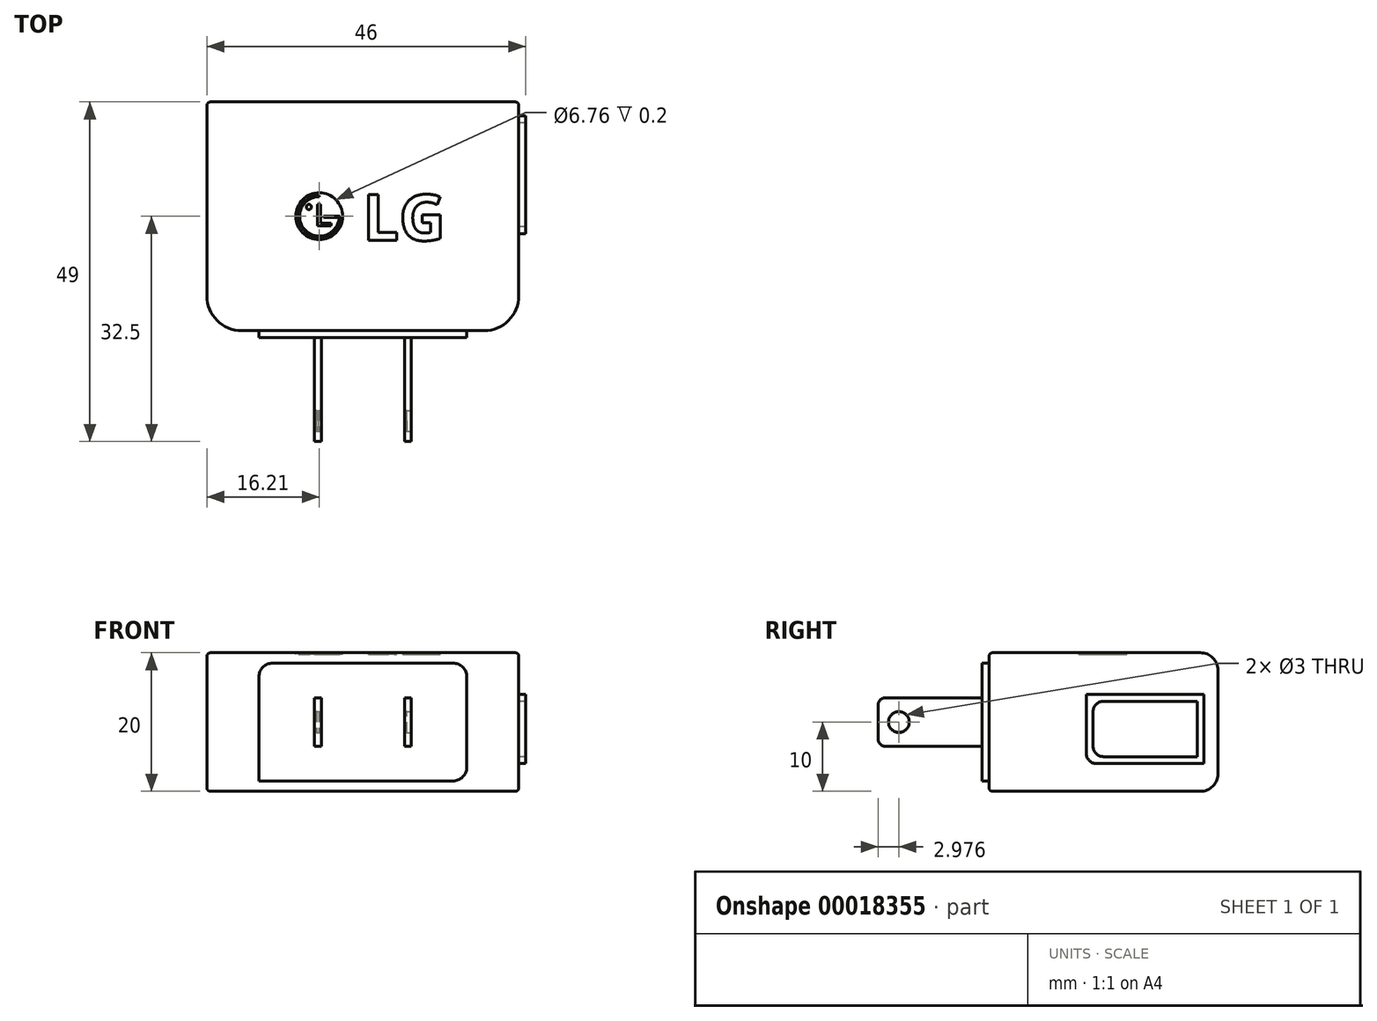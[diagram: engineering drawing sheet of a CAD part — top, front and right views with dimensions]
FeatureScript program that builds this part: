
annotation { "Feature Type Name" : "Feature", "Feature Type Description" : "" }
export const myFeature = defineFeature(function(context is Context, id is Id, definition is map)
    precondition{}
    {
        {
            var Q0;
            Q0=qCreatedBy(makeId("Top.planeOp"),FACE);
            var sketch = newSketch(context, id + "F0", { "sketchPlane" : qUnion([Q0])});
            skLineSegment(sketch, "E0.rect.bottom", {"start": v(22.5, 16.5) * mm, "end": v(-22.5, 16.5) * mm});
            skLineSegment(sketch, "E0.rect.top", {"start": v(22.5, -16.5) * mm, "end": v(-22.5, -16.5) * mm});
            skLineSegment(sketch, "E0.rect.left", {"start": v(22.5, 16.5) * mm, "end": v(22.5, -16.5) * mm});
            skLineSegment(sketch, "E0.rect.right", {"start": v(-22.5, 16.5) * mm, "end": v(-22.5, -16.5) * mm});
            skPoint(sketch, "E0.rect.middle", {"position": v(0, 0) * mm});
            skSolve(sketch);
        }
        {
            var Q0;
            Q0=makeQuery(id+"F0.imprint","IMPRINT",FACE,{"disambiguationData":[TD([[makeQuery(id+"F0.imprint","IMPRINT",EDGE,{"derivedFrom":sQuery(id+"F0.wireOp",EDGE,"E0.rect.bottom")}),1.0]])]});
            extrude(context, id + "F1", {"entities" : qUnion([Q0]), "depth" : 20 * mm});
        }
        {
            var Q0;
            Q0=makeQuery(id+"F1.opExtrude","SWEPT_FACE",FACE,{"disambiguationData":[OSD([sQuery(id+"F0.wireOp",EDGE,"E0.rect.top")])]});
            var sketch = newSketch(context, id + "F2", { "sketchPlane" : qUnion([Q0])});
            skLineSegment(sketch, "E1", {"start": v(0, 0) * mm, "end": v(0, 1.5) * mm});
            skLineSegment(sketch, "E2", {"start": v(0, 1.5) * mm, "end": v(-15, 1.5) * mm});
            skLineSegment(sketch, "E3.MirrorCS", {"start": v(0, 1.5) * mm, "end": v(15, 1.5) * mm});
            skLineSegment(sketch, "E4", {"start": v(-15, 1.5) * mm, "end": v(-15, 18.5) * mm});
            skLineSegment(sketch, "E5.MirrorCS", {"start": v(15, 1.5) * mm, "end": v(15, 18.5) * mm});
            skLineSegment(sketch, "E6", {"start": v(-15, 18.5) * mm, "end": v(15, 18.5) * mm});
            skLineSegment(sketch, "E7.bottom", {"start": v(-15, 1.5) * mm, "end": v(-7, 1.5) * mm});
            skLineSegment(sketch, "E7.left", {"start": v(-15, 1.5) * mm, "end": v(-15, 6.5) * mm});
            skLineSegment(sketch, "E8.bottom", {"start": v(-7, 6.5) * mm, "end": v(-6, 6.5) * mm});
            skLineSegment(sketch, "E8.top", {"start": v(-7, 13.5) * mm, "end": v(-6, 13.5) * mm});
            skLineSegment(sketch, "E8.left", {"start": v(-7, 6.5) * mm, "end": v(-7, 13.5) * mm});
            skLineSegment(sketch, "E8.right", {"start": v(-6, 6.5) * mm, "end": v(-6, 13.5) * mm});
            skLineSegment(sketch, "E9.MirrorCS", {"start": v(6, 6.5) * mm, "end": v(6, 13.5) * mm});
            skLineSegment(sketch, "E10.MirrorCS", {"start": v(7, 6.5) * mm, "end": v(7, 13.5) * mm});
            skLineSegment(sketch, "E11.MirrorCS", {"start": v(7, 6.5) * mm, "end": v(6, 6.5) * mm});
            skLineSegment(sketch, "E12.MirrorCS", {"start": v(7, 13.5) * mm, "end": v(6, 13.5) * mm});
            skSolve(sketch);
        }
        {
            var Q0;
            Q0=makeQuery(id+"F2.imprint","IMPRINT",FACE,{"disambiguationData":[TD([[makeQuery(id+"F2.imprint","IMPRINT",EDGE,{"derivedFrom":sQuery(id+"F2.wireOp",EDGE,"E2")}),-1.0]])]});
            extrude(context, id + "F3", {"entities" : qUnion([Q0]), "operationType" : NewBodyOperationType.ADD, "depth" : 1 * mm});
        }
        {
            var Q0;
            Q0=makeQuery(id+"F3.boolean.opBoolean","SPLIT",FACE,{"disambiguationData":[TD([makeQuery(id+"F3.opExtrude","SWEPT_FACE",FACE,{"disambiguationData":[OSD([sQuery(id+"F2.wireOp",EDGE,"E8.bottom")])]})])],"derivedFrom":makeQuery(id+"F1.opExtrude","SWEPT_FACE",FACE,{"disambiguationData":[OSD([sQuery(id+"F0.wireOp",EDGE,"E0.rect.top")])]})});
            var Q1;
            Q1=makeQuery(id+"F3.boolean.opBoolean","SPLIT",FACE,{"disambiguationData":[TD([makeQuery(id+"F3.opExtrude","SWEPT_FACE",FACE,{"disambiguationData":[OSD([sQuery(id+"F2.wireOp",EDGE,"E9.MirrorCS")])]})])],"derivedFrom":makeQuery(id+"F1.opExtrude","SWEPT_FACE",FACE,{"disambiguationData":[OSD([sQuery(id+"F0.wireOp",EDGE,"E0.rect.top")])]})});
            extrude(context, id + "F4", {"entities" : qUnion([Q0, Q1]), "operationType" : NewBodyOperationType.ADD, "depth" : 16 * mm});
        }
        {
            var Q0;
            Q0=makeQuery(id+"F4.opExtrude","CAP_EDGE",EDGE,{"disambiguationData":[OSD([sQuery(id+"F2.wireOp",EDGE,"E8.top")])],"isStart":false});
            var Q1;
            Q1=makeQuery(id+"F4.opExtrude","CAP_EDGE",EDGE,{"disambiguationData":[OSD([sQuery(id+"F2.wireOp",EDGE,"E8.bottom")])],"isStart":false});
            var Q2;
            Q2=makeQuery(id+"F4.opExtrude","CAP_EDGE",EDGE,{"disambiguationData":[OSD([sQuery(id+"F2.wireOp",EDGE,"E11.MirrorCS")])],"isStart":false});
            var Q3;
            Q3=makeQuery(id+"F4.opExtrude","CAP_EDGE",EDGE,{"disambiguationData":[OSD([sQuery(id+"F2.wireOp",EDGE,"E12.MirrorCS")])],"isStart":false});
            fillet(context, id + "F5", {"entities" : qUnion([Q0, Q1, Q2, Q3]), "radius" : 1 * mm, "tangentPropagation" : true, "allowEdgeOverflow" : false});
        }
        {
            var Q0;
            Q0=makeQuery(id+"F3.opExtrude","SWEPT_EDGE",EDGE,{"disambiguationData":[OSD([sQuery(id+"F2.wireOp",EDGE,"E5.MirrorCS"),sQuery(id+"F2.wireOp",EDGE,"E6")])]});
            var Q1;
            Q1=makeQuery(id+"F3.opExtrude","SWEPT_EDGE",EDGE,{"disambiguationData":[OSD([sQuery(id+"F2.wireOp",EDGE,"E4"),sQuery(id+"F2.wireOp",EDGE,"E6")])]});
            var Q2;
            Q2=makeQuery(id+"F3.opExtrude","SWEPT_EDGE",EDGE,{"disambiguationData":[OSD([sQuery(id+"F2.wireOp",EDGE,"E3.MirrorCS"),sQuery(id+"F2.wireOp",EDGE,"E5.MirrorCS")])]});
            var Q3;
            Q3=makeQuery(id+"F3.opExtrude","SWEPT_EDGE",EDGE,{"disambiguationData":[OSD([sQuery(id+"F2.wireOp",EDGE,"E7.bottom"),sQuery(id+"F2.wireOp",EDGE,"E7.left")])]});
            fillet(context, id + "F6", {"entities" : qUnion([Q0, Q1, Q2, Q3]), "radius" : 2 * mm, "tangentPropagation" : true, "allowEdgeOverflow" : false});
        }
        {
            var Q0;
            Q0=makeQuery(id+"F1.opExtrude","SWEPT_FACE",FACE,{"disambiguationData":[OSD([sQuery(id+"F0.wireOp",EDGE,"E0.rect.left")])]});
            var sketch = newSketch(context, id + "F7", { "sketchPlane" : qUnion([Q0])});
            skLineSegment(sketch, "E13", {"start": v(14.5, 14) * mm, "end": v(14.5, 4) * mm});
            skLineSegment(sketch, "E14", {"start": v(-2.5, 4) * mm, "end": v(14.5, 4) * mm});
            skLineSegment(sketch, "E15", {"start": v(14.5, 14) * mm, "end": v(-2.5, 14) * mm});
            skLineSegment(sketch, "E16", {"start": v(-2.5, 14) * mm, "end": v(-2.5, 4) * mm});
            skLineSegment(sketch, "E17.bottom", {"start": v(-2.5, 14) * mm, "end": v(-1.5, 14) * mm});
            skLineSegment(sketch, "E17.left", {"start": v(-2.5, 14) * mm, "end": v(-2.5, 13) * mm});
            skLineSegment(sketch, "E18.bottom", {"start": v(14.5, 4) * mm, "end": v(13.5, 4) * mm});
            skLineSegment(sketch, "E18.left", {"start": v(14.5, 4) * mm, "end": v(14.5, 5) * mm});
            skLineSegment(sketch, "E19.bottom", {"start": v(-1.5, 13) * mm, "end": v(13.5, 13) * mm});
            skLineSegment(sketch, "E19.top", {"start": v(-1.5, 5) * mm, "end": v(13.5, 5) * mm});
            skLineSegment(sketch, "E19.left", {"start": v(-1.5, 13) * mm, "end": v(-1.5, 5) * mm});
            skLineSegment(sketch, "E19.right", {"start": v(13.5, 13) * mm, "end": v(13.5, 5) * mm});
            skSolve(sketch);
        }
        {
            var Q0;
            Q0 = qSketchRegion(id + "F7", true);
            extrude(context, id + "F8", {"entities" : qUnion([Q0]), "operationType" : NewBodyOperationType.ADD, "depth" : 1 * mm});
        }
        {
            var Q0;
            Q0=makeQuery(id+"F8.opExtrude","SWEPT_EDGE",EDGE,{"disambiguationData":[OSD([sQuery(id+"F7.wireOp",EDGE,"E17.bottom"),sQuery(id+"F7.wireOp",EDGE,"E17.left")])]});
            var Q1;
            Q1=makeQuery(id+"F8.opExtrude","SWEPT_EDGE",EDGE,{"disambiguationData":[OSD([sQuery(id+"F7.wireOp",EDGE,"E14"),sQuery(id+"F7.wireOp",EDGE,"E16")])]});
            var Q2;
            Q2=makeQuery(id+"F8.opExtrude","SWEPT_EDGE",EDGE,{"disambiguationData":[OSD([sQuery(id+"F7.wireOp",EDGE,"E19.top"),sQuery(id+"F7.wireOp",EDGE,"E19.left")])]});
            var Q3;
            Q3=makeQuery(id+"F8.opExtrude","SWEPT_EDGE",EDGE,{"disambiguationData":[OSD([sQuery(id+"F7.wireOp",EDGE,"E19.bottom"),sQuery(id+"F7.wireOp",EDGE,"E19.left")])]});
            fillet(context, id + "F9", {"entities" : qUnion([Q0, Q1, Q2, Q3]), "radius" : 1.5 * mm, "tangentPropagation" : true, "allowEdgeOverflow" : false});
        }
        {
            var Q0;
            Q0=makeQuery(id+"F1.opExtrude","CAP_EDGE",EDGE,{"disambiguationData":[OSD([sQuery(id+"F0.wireOp",EDGE,"E0.rect.bottom")])],"isStart":false});
            var Q1;
            Q1=makeQuery(id+"F1.opExtrude","CAP_EDGE",EDGE,{"disambiguationData":[OSD([sQuery(id+"F0.wireOp",EDGE,"E0.rect.bottom")])],"isStart":true});
            fillet(context, id + "F10", {"entities" : qUnion([Q0, Q1]), "radius" : 2.5 * mm, "tangentPropagation" : true, "allowEdgeOverflow" : false});
        }
        {
            var Q0;
            Q0=makeQuery(id+"F1.opExtrude","SWEPT_EDGE",EDGE,{"disambiguationData":[OSD([sQuery(id+"F0.wireOp",EDGE,"E0.rect.top"),sQuery(id+"F0.wireOp",EDGE,"E0.rect.left")])]});
            var Q1;
            Q1=makeQuery(id+"F1.opExtrude","SWEPT_EDGE",EDGE,{"disambiguationData":[OSD([sQuery(id+"F0.wireOp",EDGE,"E0.rect.top"),sQuery(id+"F0.wireOp",EDGE,"E0.rect.right")])]});
            fillet(context, id + "F11", {"entities" : qUnion([Q0, Q1]), "radius" : 5 * mm, "tangentPropagation" : true, "allowEdgeOverflow" : false});
        }
        {
            var Q0;
            Q0=makeQuery(id+"F1.opExtrude","CAP_EDGE",EDGE,{"disambiguationData":[OSD([sQuery(id+"F0.wireOp",EDGE,"E0.rect.top")])],"isStart":false});
            var Q1;
            {var subQ0=sQuery(id+"F0.wireOp",EDGE,"E0.rect.top");var subQ1=sQuery(id+"F0.wireOp",EDGE,"E0.rect.left");Q1=makeQuery(id+"F11.opFillet","BLEND_EDGE",EDGE,{"blendedFrom":[makeQuery(id+"F1.opExtrude","SWEPT_EDGE",EDGE,{"disambiguationData":[OSD([subQ0,subQ1])]}),makeQuery(id+"F1.opExtrude","CAP_FACE",FACE,{"disambiguationData":[OSD([sQuery(id+"F0.wireOp",EDGE,"E0.rect.bottom"),subQ0,subQ1,sQuery(id+"F0.wireOp",EDGE,"E0.rect.right")])],"isStart":false})],"blendedInto":[makeQuery(id+"F1.opExtrude","CAP_FACE",FACE,{"disambiguationData":[OSD([sQuery(id+"F0.wireOp",EDGE,"E0.rect.bottom"),subQ0,subQ1,sQuery(id+"F0.wireOp",EDGE,"E0.rect.right")])],"isStart":false})]});}
            var Q2;
            Q2=makeQuery(id+"F1.opExtrude","CAP_EDGE",EDGE,{"disambiguationData":[OSD([sQuery(id+"F0.wireOp",EDGE,"E0.rect.left")])],"isStart":false});
            var Q3;
            Q3=makeQuery(id+"F1.opExtrude","CAP_EDGE",EDGE,{"disambiguationData":[OSD([sQuery(id+"F0.wireOp",EDGE,"E0.rect.right")])],"isStart":false});
            var Q4;
            {var subQ0=sQuery(id+"F0.wireOp",EDGE,"E0.rect.top");var subQ1=sQuery(id+"F0.wireOp",EDGE,"E0.rect.right");Q4=makeQuery(id+"F11.opFillet","BLEND_EDGE",EDGE,{"blendedFrom":[makeQuery(id+"F1.opExtrude","SWEPT_EDGE",EDGE,{"disambiguationData":[OSD([subQ0,subQ1])]}),makeQuery(id+"F1.opExtrude","CAP_FACE",FACE,{"disambiguationData":[OSD([sQuery(id+"F0.wireOp",EDGE,"E0.rect.bottom"),subQ0,sQuery(id+"F0.wireOp",EDGE,"E0.rect.left"),subQ1])],"isStart":false})],"blendedInto":[makeQuery(id+"F1.opExtrude","CAP_FACE",FACE,{"disambiguationData":[OSD([sQuery(id+"F0.wireOp",EDGE,"E0.rect.bottom"),subQ0,sQuery(id+"F0.wireOp",EDGE,"E0.rect.left"),subQ1])],"isStart":false})]});}
            var Q5;
            Q5=makeQuery(id+"F1.opExtrude","CAP_EDGE",EDGE,{"disambiguationData":[OSD([sQuery(id+"F0.wireOp",EDGE,"E0.rect.left")])],"isStart":true});
            var Q6;
            {var subQ0=sQuery(id+"F0.wireOp",EDGE,"E0.rect.top");var subQ1=sQuery(id+"F0.wireOp",EDGE,"E0.rect.left");Q6=makeQuery(id+"F11.opFillet","BLEND_EDGE",EDGE,{"blendedFrom":[makeQuery(id+"F1.opExtrude","SWEPT_EDGE",EDGE,{"disambiguationData":[OSD([subQ0,subQ1])]}),makeQuery(id+"F1.opExtrude","CAP_FACE",FACE,{"disambiguationData":[OSD([sQuery(id+"F0.wireOp",EDGE,"E0.rect.bottom"),subQ0,subQ1,sQuery(id+"F0.wireOp",EDGE,"E0.rect.right")])],"isStart":true})],"blendedInto":[makeQuery(id+"F1.opExtrude","CAP_FACE",FACE,{"disambiguationData":[OSD([sQuery(id+"F0.wireOp",EDGE,"E0.rect.bottom"),subQ0,subQ1,sQuery(id+"F0.wireOp",EDGE,"E0.rect.right")])],"isStart":true})]});}
            var Q7;
            Q7=makeQuery(id+"F1.opExtrude","CAP_EDGE",EDGE,{"disambiguationData":[OSD([sQuery(id+"F0.wireOp",EDGE,"E0.rect.top")])],"isStart":true});
            var Q8;
            {var subQ0=sQuery(id+"F0.wireOp",EDGE,"E0.rect.top");var subQ1=sQuery(id+"F0.wireOp",EDGE,"E0.rect.right");Q8=makeQuery(id+"F11.opFillet","BLEND_EDGE",EDGE,{"blendedFrom":[makeQuery(id+"F1.opExtrude","SWEPT_EDGE",EDGE,{"disambiguationData":[OSD([subQ0,subQ1])]}),makeQuery(id+"F1.opExtrude","CAP_FACE",FACE,{"disambiguationData":[OSD([sQuery(id+"F0.wireOp",EDGE,"E0.rect.bottom"),subQ0,sQuery(id+"F0.wireOp",EDGE,"E0.rect.left"),subQ1])],"isStart":true})],"blendedInto":[makeQuery(id+"F1.opExtrude","CAP_FACE",FACE,{"disambiguationData":[OSD([sQuery(id+"F0.wireOp",EDGE,"E0.rect.bottom"),subQ0,sQuery(id+"F0.wireOp",EDGE,"E0.rect.left"),subQ1])],"isStart":true})]});}
            var Q9;
            Q9=makeQuery(id+"F1.opExtrude","CAP_EDGE",EDGE,{"disambiguationData":[OSD([sQuery(id+"F0.wireOp",EDGE,"E0.rect.right")])],"isStart":true});
            fillet(context, id + "F12", {"entities" : qUnion([Q0, Q1, Q2, Q3, Q4, Q5, Q6, Q7, Q8, Q9]), "radius" : 0.5 * mm, "tangentPropagation" : true, "allowEdgeOverflow" : false});
        }
        {
            var Q0;
            Q0=makeQuery(id+"F4.opExtrude","SWEPT_FACE",FACE,{"disambiguationData":[OSD([sQuery(id+"F2.wireOp",EDGE,"E10.MirrorCS")])]});
            var sketch = newSketch(context, id + "F13", { "sketchPlane" : qUnion([Q0])});
            skCircle(sketch, "E20", {"center": v(-29.52, 10) * mm, "radius": 1.5 * mm});
            skSolve(sketch);
        }
        {
            var Q0;
            Q0=makeQuery(id+"F13.imprint","IMPRINT",FACE,{"disambiguationData":[TD([[makeQuery(id+"F13.imprint","IMPRINT",EDGE,{"derivedFrom":sQuery(id+"F13.wireOp",EDGE,"E20")}),1.0]])]});
            extrude(context, id + "F14", {"entities" : qUnion([Q0]), "operationType" : NewBodyOperationType.REMOVE, "oppositeDirection" : true, "depth" : 25 * mm});
        }
        {
            var Q0;
            Q0=makeQuery(id+"F14.boolean.opBoolean","INTERSECT",EDGE,{"derivedFrom":[makeQuery(id+"F4.opExtrude","SWEPT_FACE",FACE,{"disambiguationData":[OSD([sQuery(id+"F2.wireOp",EDGE,"E8.left")])]}),makeQuery(id+"F14.opExtrude","SWEPT_FACE",FACE,{"disambiguationData":[OSD([sQuery(id+"F13.wireOp",EDGE,"E20")])]})]});
            var Q1;
            Q1=makeQuery(id+"F14.boolean.opBoolean","INTERSECT",EDGE,{"derivedFrom":[makeQuery(id+"F4.opExtrude","SWEPT_FACE",FACE,{"disambiguationData":[OSD([sQuery(id+"F2.wireOp",EDGE,"E8.right")])]}),makeQuery(id+"F14.opExtrude","SWEPT_FACE",FACE,{"disambiguationData":[OSD([sQuery(id+"F13.wireOp",EDGE,"E20")])]})]});
            var Q2;
            Q2=makeQuery(id+"F14.boolean.opBoolean","INTERSECT",EDGE,{"derivedFrom":[makeQuery(id+"F4.opExtrude","SWEPT_FACE",FACE,{"disambiguationData":[OSD([sQuery(id+"F2.wireOp",EDGE,"E9.MirrorCS")])]}),makeQuery(id+"F14.opExtrude","SWEPT_FACE",FACE,{"disambiguationData":[OSD([sQuery(id+"F13.wireOp",EDGE,"E20")])]})]});
            var Q3;
            Q3=makeQuery(id+"F14.boolean.opBoolean","COPY",EDGE,{"derivedFrom":makeQuery(id+"F14.opExtrude","CAP_EDGE",EDGE,{"disambiguationData":[OSD([sQuery(id+"F13.wireOp",EDGE,"E20")])],"isStart":true})});
            chamfer(context, id + "F15", {"entities" : qUnion([Q0, Q1, Q2, Q3]), "chamferType" : ChamferType.TWO_OFFSETS, "width1" : 0.35 * mm, "oppositeDirection" : false, "width2" : 0.1 * mm, "tangentPropagation" : true});
        }
        {
            var Q0;
            Q0=makeQuery(id+"F1.opExtrude","CAP_FACE",FACE,{"disambiguationData":[OSD([sQuery(id+"F0.wireOp",EDGE,"E0.rect.bottom"),sQuery(id+"F0.wireOp",EDGE,"E0.rect.top"),sQuery(id+"F0.wireOp",EDGE,"E0.rect.left"),sQuery(id+"F0.wireOp",EDGE,"E0.rect.right")])],"isStart":false});
            var sketch = newSketch(context, id + "F16", { "sketchPlane" : qUnion([Q0])});
            skText(sketch, "E21", { "text": "LG", "fontName": "OpenSans-Bold.ttf"});
            skCircle(sketch, "E22", {"center": v(-6.29, 0) * mm, "radius": 3.38 * mm});
            skLineSegment(sketch, "E23", {"start": v(-6.29, 0) * mm, "end": v(-6.29, 3) * mm});
            skLineSegment(sketch, "E24", {"start": v(-6.29, 0) * mm, "end": v(-3.29, 0) * mm});
            skArc(sketch, "E25", {"start": v(-6.29, 3) * mm, "mid": v(-8.4, -2.12) * mm, "end": v(-3.29, 0) * mm});
            skArc(sketch, "E26", {"start": v(-6.29, 2.84) * mm, "mid": v(-8.28, -2.03) * mm, "end": v(-3.43, 0) * mm});
            skText(sketch, "E27", { "text": "L", "fontName": "Arimo-Regular.ttf"});
            skLineSegment(sketch, "E28.bottom", {"start": v(-3.3, -0.18) * mm, "end": v(-5.64, -0.18) * mm});
            skLineSegment(sketch, "E28.top", {"start": v(-3.3, 0) * mm, "end": v(-5.64, 0) * mm});
            skLineSegment(sketch, "E28.left", {"start": v(-3.3, -0.18) * mm, "end": v(-3.3, 0) * mm});
            skLineSegment(sketch, "E28.right", {"start": v(-5.64, -0.18) * mm, "end": v(-5.64, 0) * mm});
            skCircle(sketch, "E29", {"center": v(-7.8, 1.34) * mm, "radius": 0.37 * mm});
            const initialGuessF16  = {"E21": [0, -0.00349, 1, 0, 0.00665], "E27": [-0.0069, -0.00135, 1, 0, 0.0032]};
            skSetInitialGuess(sketch, initialGuessF16);
            skSolve(sketch);
        }
        {
            var Q0;
            Q0=makeQuery(id+"F16.imprint","IMPRINT",FACE,{"disambiguationData":[TD([[makeQuery(id+"F16.imprint","IMPRINT",EDGE,{"derivedFrom":sQuery(id+"F16.wireOp",EDGE,"E21.sketch_text.stroke-0")}),-1.0]])]});
            var Q1;
            Q1=makeQuery(id+"F16.imprint","IMPRINT",FACE,{"disambiguationData":[TD([[makeQuery(id+"F16.imprint","IMPRINT",EDGE,{"derivedFrom":sQuery(id+"F16.wireOp",EDGE,"E21.sketch_text.stroke-6")}),-1.0]])]});
            extrude(context, id + "F17", {"entities" : qUnion([Q0, Q1]), "operationType" : NewBodyOperationType.REMOVE, "oppositeDirection" : true, "depth" : 0.2 * mm});
        }
        {
            var Q0;
            Q0=makeQuery(id+"F16.imprint","IMPRINT",FACE,{"disambiguationData":[TD([[makeQuery(id+"F16.imprint","IMPRINT",EDGE,{"derivedFrom":sQuery(id+"F16.wireOp",EDGE,"E22")}),1.0]])]});
            var Q1;
            {var subQ11=sQuery(id+"F16.wireOp",EDGE,"E27.sketch_text.stroke-0");Q1=makeQuery(id+"F16.imprint","IMPRINT",FACE,{"disambiguationData":[TD([[makeQuery(id+"F16.imprint","IMPRINT",EDGE,{"derivedFrom":subQ11}),1.0]])]});}
            extrude(context, id + "F18", {"entities" : qUnion([Q0, Q1]), "operationType" : NewBodyOperationType.REMOVE, "oppositeDirection" : true, "depth" : 0.2 * mm});
        }
    });
